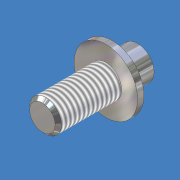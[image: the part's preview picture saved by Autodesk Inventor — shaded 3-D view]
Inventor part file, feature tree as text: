
AUTODESK INVENTOR PART (.ipt)
format: ipt  version: 2012 (Build 160160000, 160)  size: 104,448 bytes
history: native  units: mm (DEFAULTED — no unit token found)
features: extrude x3, sketch x3, chamfer x1, thread x1
ambient origin geometry x8: Origin, YZ Plane, XZ Plane, XY Plane, X Axis, Y Axis, Z Axis, Center Point
bodies: Solid1 (feature_tree)
feature tree (8):
  extrude  "Extrusion1"  Depth=1.27mm TaperAngle=0.0deg
  extrude  "Extrusion2"  Depth=12.7mm TaperAngle=0.0deg
  chamfer  "Chamfer1"  Distance=0.635mm
  thread  "Thread1"  [1 undecoded]
  extrude  "Extrusion3"  Depth=5.08mm TaperAngle=0.0deg
  sketch  "Sketch1"  dims[d0=12.7mm d1=1.27mm d2=0.0mm]
  sketch  "Sketch2"  dims[d3=6.35mm d4=12.7mm d5=0.0mm d6=0.635mm d7=0.635mm d8=25.4mm d9=0.0mm]
  sketch  "Sketch3"  dims[d10=6.604mm d11=5.08mm d12=0.0mm d13=45.0deg]
note: 1 required parameter value undecoded (feature->parameter linkage not recoverable at this tier; creation-order binding heuristic only, values carry confidence <= 0.55)
